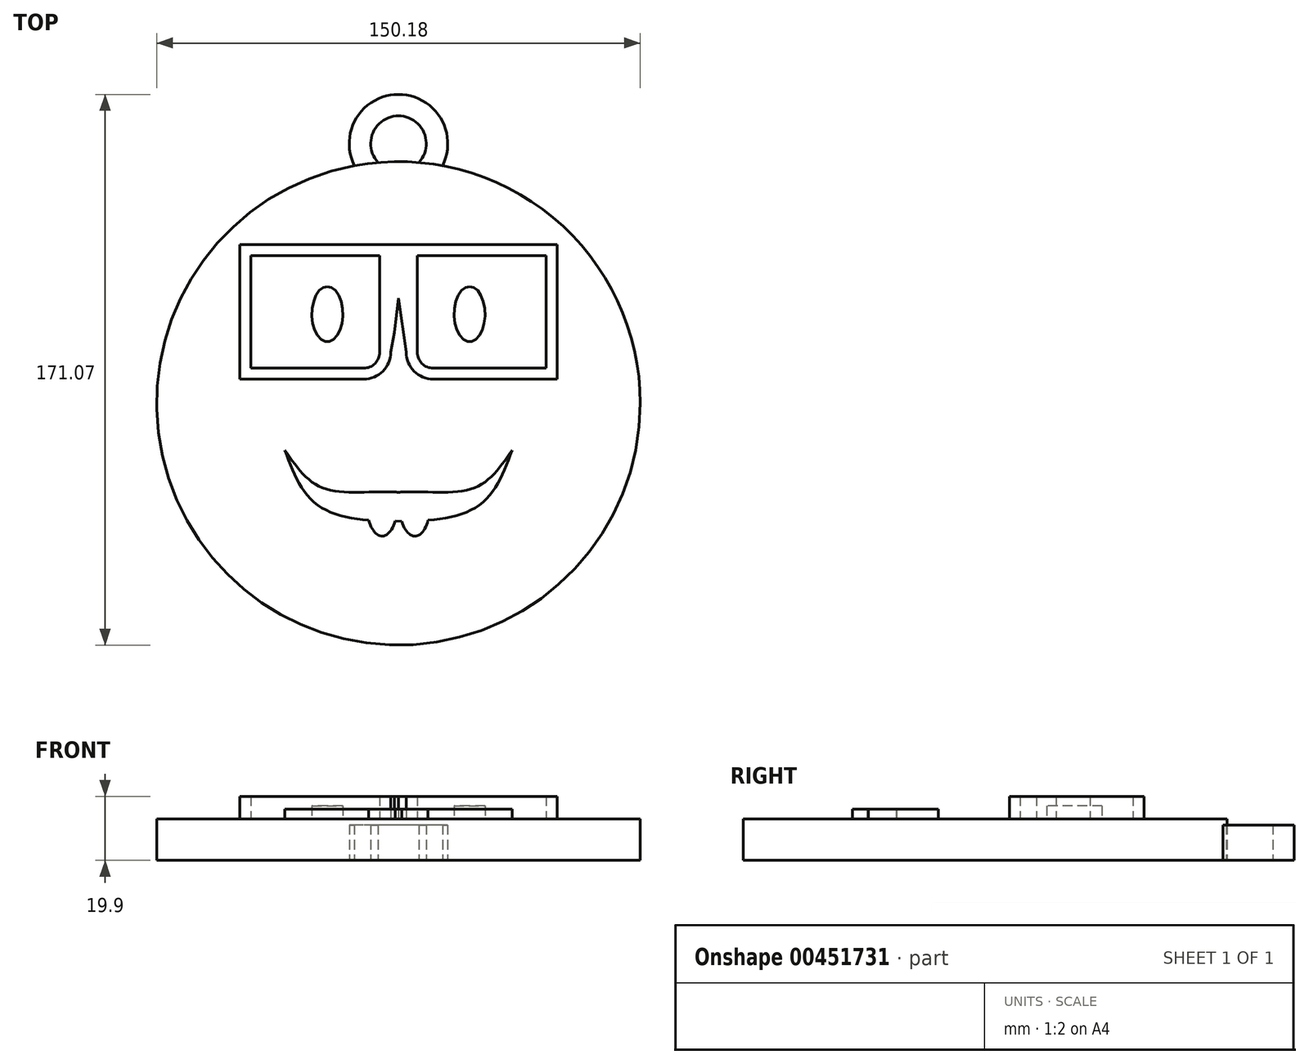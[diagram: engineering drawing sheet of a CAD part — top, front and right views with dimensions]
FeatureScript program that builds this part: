
annotation { "Feature Type Name" : "Feature", "Feature Type Description" : "" }
export const myFeature = defineFeature(function(context is Context, id is Id, definition is map)
    precondition{}
    {
        {
            var Q0;
            Q0=qCreatedBy(makeId("Top.planeOp"),FACE);
            var sketch = newSketch(context, id + "F0", { "sketchPlane" : qUnion([Q0])});
            skCircle(sketch, "E0", {"center": v(0, 0) * mm, "radius": 75.1 * mm});
            skSolve(sketch);
        }
        {
            var Q0;
            Q0=makeQuery(id+"F0.imprint","IMPRINT",FACE,{"disambiguationData":[TD([[makeQuery(id+"F0.imprint","IMPRINT",EDGE,{"derivedFrom":sQuery(id+"F0.wireOp",EDGE,"E0")}),1.0]])]});
            var sketch = newSketch(context, id + "F1", { "sketchPlane" : qUnion([Q0])});
            skFitSpline(sketch, "E1", {"points": [v(-35.25, -14.53) * mm, v(-25.07, -31.61) * mm, v(0, -36.15) * mm], "startDerivative": vector(15.57, -43.86) * mm, "endDerivative": vector(54.17, 4.4) * mm});
            skFitSpline(sketch, "E2", {"points": [v(-35.25, -14.53) * mm, v(-23.8, -26.16) * mm, v(0, -27.61) * mm], "startDerivative": vector(21.16, -30.9) * mm, "endDerivative": vector(49.8, -2.99) * mm});
            skFitSpline(sketch, "E3.MirrorCS", {"points": [v(35.25, -14.53) * mm, v(23.8, -26.16) * mm, v(0, -27.61) * mm], "startDerivative": vector(-21.16, -30.9) * mm, "endDerivative": vector(-49.8, -2.99) * mm});
            skFitSpline(sketch, "E4.MirrorCS", {"points": [v(35.25, -14.53) * mm, v(25.07, -31.61) * mm, v(0, -36.15) * mm], "startDerivative": vector(-15.57, -43.86) * mm, "endDerivative": vector(-54.17, 4.4) * mm});
            skEllipticalArc(sketch, "E5", {});
            skEllipticalArc(sketch, "E6.MirrorCS", {});
            skEllipticalArc(sketch, "E7.trimOffspring", {});
            skLineSegment(sketch, "E8", {"start": v(9.59, -36.93) * mm, "end": v(9.04, -36.91) * mm});
            skLineSegment(sketch, "E9.trimOffspring", {"start": v(1.06, -36.64) * mm, "end": v(-1.04, -36.57) * mm});
            const initialGuessF1  = {"E5": [-0.005086933262646198, -0.03215668722987175, 0, 1, 0.009083809331059456, 0.0046355675826284855, 1.0400212004337883, 2.043901218676275], "E6.MirrorCS": [0.005086933262646198, -0.03215668722987175, 0, 1, 0.009083809331059456, 0.0046355675826284855, 1.040122318514026, 5.243164106745798], "E7.trimOffspring": [-0.005086933262646198, -0.03215668722987175, 0, 1, 0.009083809331059456, 0.0046355675826284855, 2.043901218676275, 5.24306298866556]};
            skSetInitialGuess(sketch, initialGuessF1);
            skSolve(sketch);
        }
        {
            var Q0;
            Q0=makeQuery(id+"F0.imprint","IMPRINT",FACE,{"disambiguationData":[TD([[makeQuery(id+"F0.imprint","IMPRINT",EDGE,{"derivedFrom":sQuery(id+"F0.wireOp",EDGE,"E0")}),1.0]])]});
            extrude(context, id + "F2", {"entities" : qUnion([Q0]), "depth" : 12.9 * mm});
        }
        {
            var Q0;
            Q0 = qSketchRegion(id + "F1", true);
            extrude(context, id + "F3", {"entities" : qUnion([Q0]), "operationType" : NewBodyOperationType.ADD, "depth" : 15.9 * mm});
        }
        {
            var Q0;
            {var subQ0=sQuery(id+"F0.wireOp",EDGE,"E0");Q0=makeQuery(id+"FJBbnFLUgWYsMN8_1.boolean.opBoolean","SPLIT",FACE,{"disambiguationData":[TD([makeQuery(id+"F2.opExtrude","SWEPT_FACE",FACE,{"disambiguationData":[OSD([subQ0])]})])],"derivedFrom":makeQuery(id+"F2.opExtrude","CAP_FACE",FACE,{"disambiguationData":[OSD([subQ0])],"isStart":false})});}
            var sketch = newSketch(context, id + "F4", { "sketchPlane" : qUnion([Q0])});
            skEllipse(sketch, "E10", {"center": v(-22.08, 27.72) * mm, "majorRadius": 8.57 * mm, "minorRadius": 4.8 * mm, "majorAxis": v(0, 1)});
            skEllipse(sketch, "E11.MirrorC", {"center": v(22.08, 27.72) * mm, "majorRadius": 8.57 * mm, "minorRadius": 4.8 * mm, "majorAxis": v(0, 1)});
            skSolve(sketch);
        }
        {
            var Q0;
            Q0 = qSketchRegion(id + "F4", true);
            extrude(context, id + "F5", {"entities" : qUnion([Q0]), "operationType" : NewBodyOperationType.ADD, "depth" : 4 * mm});
        }
        {
            var Q0;
            Q0=qCreatedBy(makeId("Top.planeOp"),FACE);
            var sketch = newSketch(context, id + "F6", { "sketchPlane" : qUnion([Q0])});
            skCircle(sketch, "E12", {"center": v(0, 80.68) * mm, "radius": 15.3 * mm});
            skCircle(sketch, "E13", {"center": v(0, 80.68) * mm, "radius": 8.63 * mm});
            skSolve(sketch);
        }
        {
            var Q0;
            Q0=makeQuery(id+"F6.imprint","IMPRINT",FACE,{"disambiguationData":[TD([[makeQuery(id+"F6.imprint","IMPRINT",EDGE,{"derivedFrom":sQuery(id+"F6.wireOp",EDGE,"E12")}),1.0]])]});
            extrude(context, id + "F7", {"entities" : qUnion([Q0]), "operationType" : NewBodyOperationType.ADD, "depth" : 11 * mm});
        }
        {
            var Q0;
            Q0=makeQuery(id+"F2.opExtrude","CAP_FACE",FACE,{"disambiguationData":[OSD([sQuery(id+"F0.wireOp",EDGE,"E0")])],"isStart":false});
            var sketch = newSketch(context, id + "F8", { "sketchPlane" : qUnion([Q0])});
            skLineSegment(sketch, "E14.bottom", {"start": v(-45.82, 45.93) * mm, "end": v(-5.82, 45.93) * mm});
            skLineSegment(sketch, "E14.top", {"start": v(-45.82, 10.93) * mm, "end": v(-10.82, 10.93) * mm});
            skLineSegment(sketch, "E14.left", {"start": v(-45.82, 45.93) * mm, "end": v(-45.82, 10.93) * mm});
            skLineSegment(sketch, "E14.right", {"start": v(-5.82, 45.93) * mm, "end": v(-5.82, 15.93) * mm});
            skPoint(sketch, "E15.visualSharp", {"position": v(-5.82, 10.93) * mm});
            skArc(sketch, "E15.filletArc", {"start": v(-10.82, 10.93) * mm, "mid": v(-7.28, 12.4) * mm, "end": v(-5.82, 15.93) * mm});
            skLineSegment(sketch, "E16.1", {"start": v(-49.22, 49.33) * mm, "end": v(-2.42, 49.33) * mm});
            skArc(sketch, "E16.2", {"start": v(-10.82, 7.53) * mm, "mid": v(-4.88, 9.99) * mm, "end": v(-2.42, 15.93) * mm});
            skLineSegment(sketch, "E16.3", {"start": v(-49.22, 7.53) * mm, "end": v(-10.82, 7.53) * mm});
            skLineSegment(sketch, "E16.4", {"start": v(-49.22, 49.33) * mm, "end": v(-49.22, 7.53) * mm});
            skLineSegment(sketch, "E17.MirrorCS", {"start": v(5.82, 45.93) * mm, "end": v(5.82, 15.93) * mm});
            skArc(sketch, "E18.MirrorCS", {"start": v(10.82, 7.53) * mm, "mid": v(4.88, 9.99) * mm, "end": v(2.42, 15.93) * mm});
            skArc(sketch, "E19.MirrorCS", {"start": v(10.82, 10.93) * mm, "mid": v(7.28, 12.4) * mm, "end": v(5.82, 15.93) * mm});
            skLineSegment(sketch, "E20.MirrorCS", {"start": v(49.22, 7.53) * mm, "end": v(10.82, 7.53) * mm});
            skLineSegment(sketch, "E21.MirrorCS", {"start": v(45.82, 10.93) * mm, "end": v(10.82, 10.93) * mm});
            skLineSegment(sketch, "E22.MirrorCS", {"start": v(49.22, 49.33) * mm, "end": v(49.22, 7.53) * mm});
            skLineSegment(sketch, "E23.MirrorCS", {"start": v(45.82, 45.93) * mm, "end": v(45.82, 10.93) * mm});
            skLineSegment(sketch, "E24.MirrorCS", {"start": v(49.22, 49.33) * mm, "end": v(2.42, 49.33) * mm});
            skLineSegment(sketch, "E25.MirrorCS", {"start": v(45.82, 45.93) * mm, "end": v(5.82, 45.93) * mm});
            skLineSegment(sketch, "E26", {"start": v(-1.2, 22) * mm, "end": v(0, 32.63) * mm});
            skPoint(sketch, "E26.endSnap0", {"position": v(-2.42, 32.63) * mm});
            skLineSegment(sketch, "E27", {"start": v(0, 32.63) * mm, "end": v(2.42, 15.93) * mm});
            skLineSegment(sketch, "E28", {"start": v(-2.42, 49.33) * mm, "end": v(2.42, 49.33) * mm});
            skPoint(sketch, "E29.MirrorCS.end.orphan", {"position": v(2.42, 15.93) * mm});
            skLineSegment(sketch, "E30", {"start": v(-2.42, 15.93) * mm, "end": v(-1.2, 22) * mm});
            skPoint(sketch, "E16.0.start.orphan", {"position": v(-2.42, 11.37) * mm});
            skSolve(sketch);
        }
        {
            var Q0;
            Q0 = qSketchRegion(id + "F8", true);
            extrude(context, id + "F9", {"entities" : qUnion([Q0]), "operationType" : NewBodyOperationType.ADD, "depth" : 7 * mm});
        }
    });
